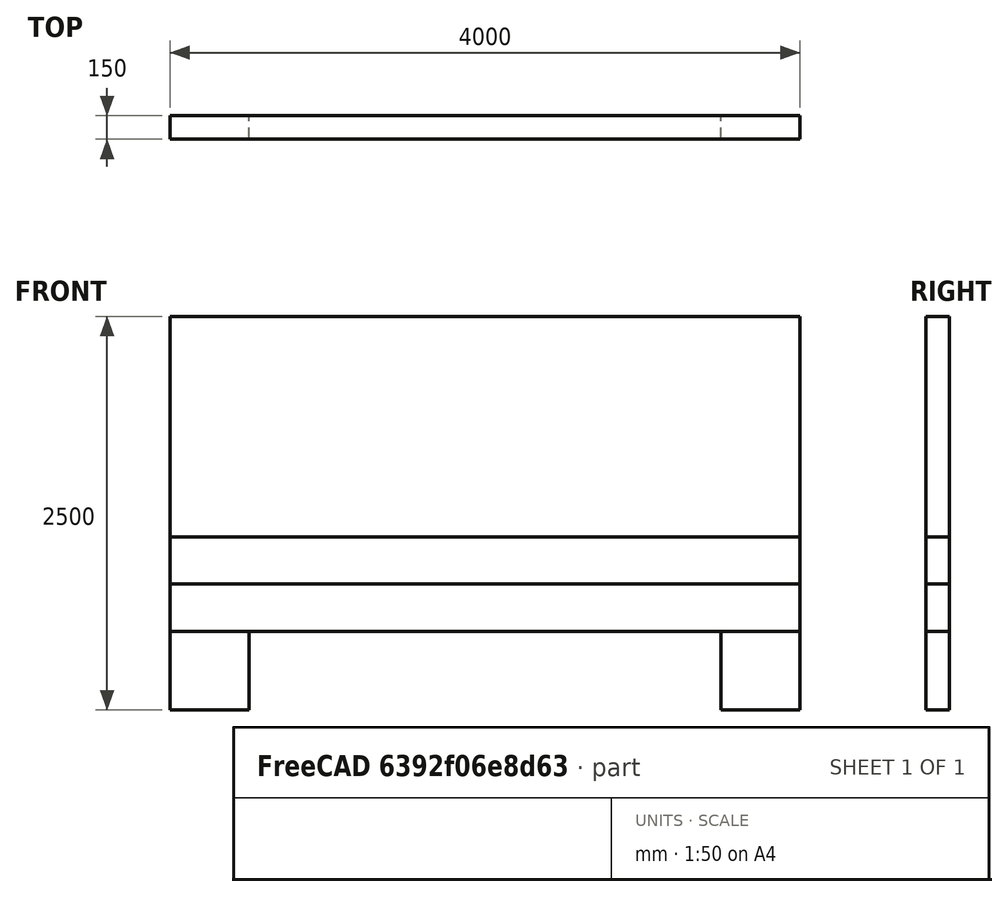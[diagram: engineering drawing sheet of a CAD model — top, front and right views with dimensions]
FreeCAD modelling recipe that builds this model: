
FCSTD DOCUMENT  (FreeCAD 0.21R33694 (Git))
Label: wall_tutorial
License: All rights reserved
LicenseURL: http://en.wikipedia.org/wiki/All_rights_reserved
objects: Part::Box×5, App::MaterialObjectPython×3, Fem::ConstraintForce×1, Fem::ConstraintFixed×1, Fem::FemSolverObjectPython×1, Part::FeaturePython×1, Fem::FemMeshObjectPython×1, Fem::ConstraintDisplacement×1, Fem::FemAnalysis×1
note: 6 computed .brp shape members not serialized (recipe doc carries the construction recipe); baked Part::Feature solids carry a one-line shape summary decoded from their .brp

FEATURE [Part::Box] Box  label="Cube"
  AttacherType = Attacher::AttachEngine3D
  Height = 1400
  Length = 4000
  Placement = pos=(0,0,600) rot=(0,0,1;0rad)
  Width = 150
FEATURE [Part::Box] Box001  label="Cube001"
  AttacherType = Attacher::AttachEngine3D
  Height = 500
  Length = 500
  Placement = pos=(0,0,-500) rot=(0,0,1;0rad)
  Width = 150
FEATURE [Part::Box] Box002  label="Cube002"
  AttacherType = Attacher::AttachEngine3D
  Height = 500
  Length = 500
  Placement = pos=(3500,0,-500) rot=(0,0,1;0rad)
  Width = 150
FEATURE [Fem::ConstraintForce] ConstraintForce
  DirectionVector = (0,0,-1)
  Force = 1000000
  NormalDirection = (0,0,1)
  Points = (40) [(0,0,2000),(444.444,0,2000),(888.889,0,2000),(1333.33,0,2000),(1777.78,0,2000),(2222.22,0,2000),(2666.67,0,2000),(3111.11,0,2000),(3555.56,0,2000),+31 more]
  References = -> [Box]
  Reversed = true
  Scale = 45
FEATURE [Fem::ConstraintFixed] ConstraintFixed
  NormalDirection = (0,0,-1)
  Normals = (16) [(0,0,-1),(0,0,-1),(0,0,-1),(0,0,-1),(0,0,-1),(0,0,-1),(0,0,-1),(0,0,-1),(0,0,-1),(0,0,-1),(0,0,-1),(0,0,-1),(0,0,-1),(0,0,-1),(0,0,-1),(0,0,-1)]
  Points = (16) [(0,0,-500),(166.667,0,-500),(333.333,0,-500),(500,0,-500),(0,50,-500),(166.667,50,-500),(333.333,50,-500),(500,50,-500),(0,100,-500),+7 more]
  References = -> [Box001]
  Scale = 19
FEATURE [Fem::FemSolverObjectPython] SolverCcxTools  # FEM object (typed FeaturePython)
  AnalysisType = 0
  BeamShellResultOutput3D = false
  BucklingFactors = 1
  EigenmodeHighLimit = 1000000
  EigenmodeLowLimit = 0
  EigenmodesCount = 10
  GeometricalNonlinearity = 0
  IterationsControlParameterCutb = 0.25,0.5,0.75,0.85,,,1.5,
  IterationsControlParameterIter = 4,8,9,200,10,400,,200,,
  IterationsControlParameterTimeUse = false
  IterationsThermoMechMaximum = 2000
  IterationsUserDefinedIncrementations = false
  IterationsUserDefinedTimeStepLength = false
  MaterialNonlinearity = 0
  MatrixSolverType = 0
  SplitInputWriter = false
  ThermoMechSteadyState = true
  TimeEnd = 1
  TimeInitialStep = 0.01
FEATURE [Part::Box] Box003  label="Cube003"
  AttacherType = Attacher::AttachEngine3D
  Height = 300
  Length = 4000
  Width = 150
FEATURE [Part::Box] Box004  label="Cube004"
  AttacherType = Attacher::AttachEngine3D
  Height = 300
  Length = 4000
  Placement = pos=(0,0,300) rot=(0,0,1;0rad)
  Width = 150
FEATURE [Part::FeaturePython] BooleanFragments  # WARN: FeaturePython — macro-defined, semantics opaque (R4)
  Mode = 2
  Objects = -> [Box,Box001,Box002,Box003,Box004]
  Tolerance = 0
FEATURE [App::MaterialObjectPython] MaterialSolid  label="rhox_0.0035"  # material (typed FeaturePython)
  Category = 0
  Material = AuthorAndLicense=(c) 2013 Yorik van Havre (CC-BY 3.0),CardName=Concrete-Generic,CompressiveStrength=25 MPa,Density=2400 kg/m^3,+7 more (map truncated)
  References = -> [BooleanFragments]
FEATURE [Fem::FemMeshObjectPython] FEMMeshGmsh  # FEM object (typed FeaturePython)
  Algorithm2D = 0
  Algorithm3D = 0
  CharacteristicLengthMax = 200
  CharacteristicLengthMin = 0
  CoherenceMesh = true
  ElementDimension = 0
  ElementOrder = 1
  GeometryTolerance = 1e-06
  GroupsOfNodes = false
  HighOrderOptimize = 0
  MeshSizeFromCurvature = 12
  OptimizeNetgen = false
  OptimizeStd = true
  Part = -> BooleanFragments
  RecombinationAlgorithm = 0
  Recombine3DAll = false
  RecombineAll = false
  SecondOrderLinear = false
FEATURE [App::MaterialObjectPython] MaterialSolid001  label="rhox_0.0070"  # material (typed FeaturePython)
  Category = 0
  Material = AuthorAndLicense=(c) 2013 Yorik van Havre (CC-BY 3.0),CardName=Concrete-Generic,CompressiveStrength=25 MPa,Density=2400 kg/m^3,+7 more (map truncated)
  References = -> [BooleanFragments]
FEATURE [App::MaterialObjectPython] MaterialSolid002  label="rhox_0.0140"  # material (typed FeaturePython)
  Category = 0
  Material = AuthorAndLicense=(c) 2013 Yorik van Havre (CC-BY 3.0),CardName=Concrete-Generic,CompressiveStrength=25 MPa,Density=2400 kg/m^3,+7 more (map truncated)
  References = -> [BooleanFragments]
FEATURE [Fem::ConstraintDisplacement] ConstraintDisplacement
  NormalDirection = (0,0,-1)
  Normals = (16) [(0,0,-1),(0,0,-1),(0,0,-1),(0,0,-1),(0,0,-1),(0,0,-1),(0,0,-1),(0,0,-1),(0,0,-1),(0,0,-1),(0,0,-1),(0,0,-1),(0,0,-1),(0,0,-1),(0,0,-1),(0,0,-1)]
  Points = (16) [(3500,0,-500),(3666.67,0,-500),(3833.33,0,-500),(4000,0,-500),(3500,50,-500),(3666.67,50,-500),(3833.33,50,-500),(4000,50,-500),(3500,100,-500),+7 more]
  References = -> [BooleanFragments]
  Scale = 19
  hasXFormula = false
  hasYFormula = false
  hasZFormula = false
  rotxFix = false
  rotxFree = true
  rotyFix = false
  rotyFree = true
  rotzFix = false
  rotzFree = true
  useFlowSurfaceForce = false
  xDisplacement = 0
  xFix = false
  xFree = true
  xRotation = 0
  yDisplacement = 0
  yFix = false
  yFree = false
  yRotation = 0
  zDisplacement = 0
  zFix = false
  zFree = false
  zRotation = 0
FEATURE [Fem::FemAnalysis] Analysis
  Group = -> [MaterialSolid,ConstraintForce,ConstraintFixed,SolverCcxTools,FEMMeshGmsh,MaterialSolid001,MaterialSolid002,ConstraintDisplacement]
